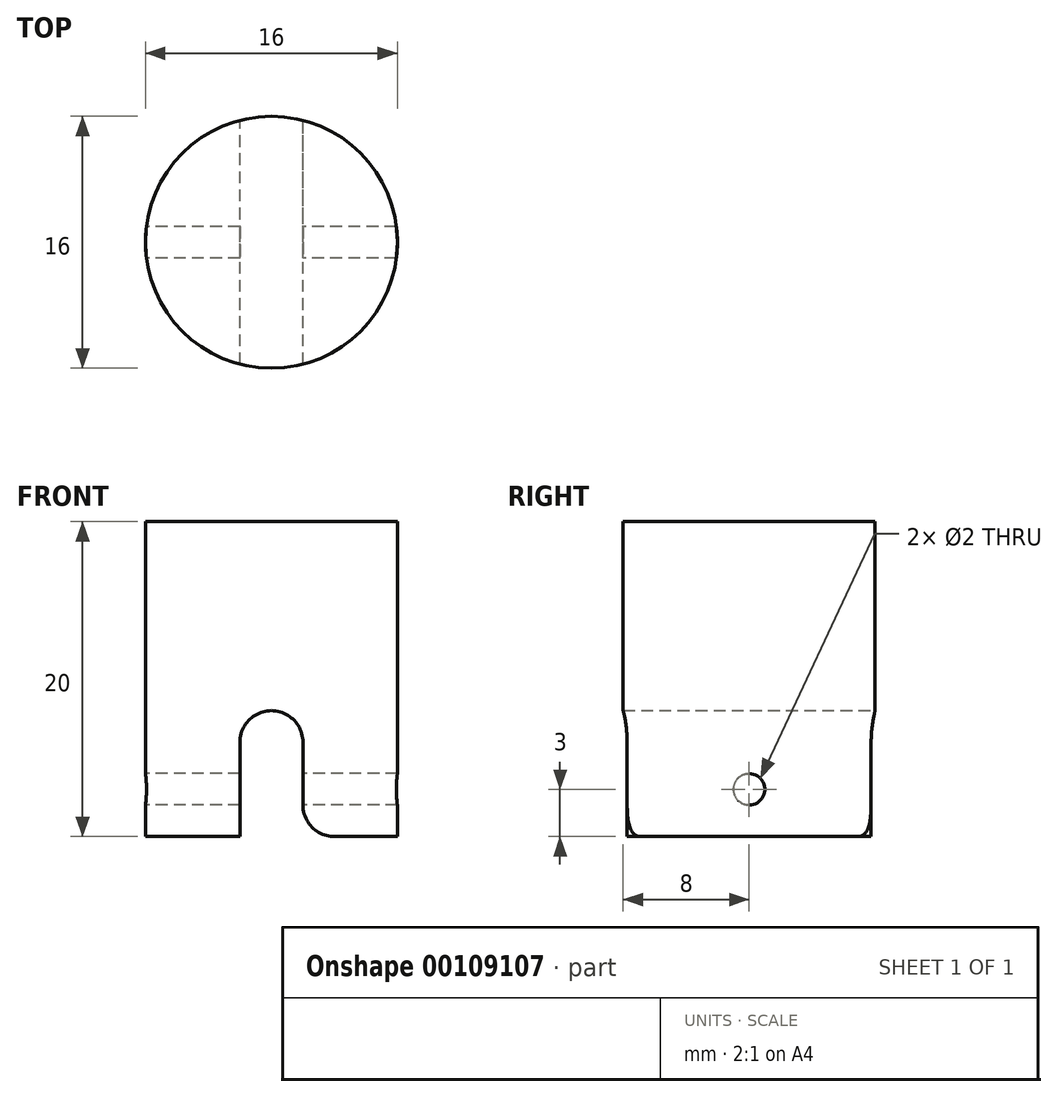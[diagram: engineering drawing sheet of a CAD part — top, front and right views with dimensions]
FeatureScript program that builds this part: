
annotation { "Feature Type Name" : "Feature", "Feature Type Description" : "" }
export const myFeature = defineFeature(function(context is Context, id is Id, definition is map)
    precondition{}
    {
        {
            var Q0;
            Q0=qCreatedBy(makeId("Top.planeOp"),FACE);
            var sketch = newSketch(context, id + "F0", { "sketchPlane" : qUnion([Q0])});
            skLineSegment(sketch, "E0.bottom", {"start": v(-8, 8) * mm, "end": v(8, 8) * mm});
            skLineSegment(sketch, "E0.top", {"start": v(-8, -8) * mm, "end": v(8, -8) * mm});
            skLineSegment(sketch, "E0.left", {"start": v(-8, 8) * mm, "end": v(-8, -8) * mm});
            skLineSegment(sketch, "E0.right", {"start": v(8, 8) * mm, "end": v(8, -8) * mm});
            skPoint(sketch, "E0.middle", {"position": v(0, 0) * mm});
            skSolve(sketch);
        }
        {
            var Q0;
            Q0=makeQuery(id+"F0.imprint","IMPRINT",FACE,{"disambiguationData":[TD([[makeQuery(id+"F0.imprint","IMPRINT",EDGE,{"derivedFrom":sQuery(id+"F0.wireOp",EDGE,"E0.bottom")}),-1.0]])]});
            extrude(context, id + "F1", {"entities" : qUnion([Q0]), "depth" : 20 * mm});
        }
        {
            var Q0;
            Q0=makeQuery(id+"F1.opExtrude","SWEPT_FACE",FACE,{"disambiguationData":[OSD([sQuery(id+"F0.wireOp",EDGE,"E0.left")])]});
            var sketch = newSketch(context, id + "F2", { "sketchPlane" : qUnion([Q0])});
            skLineSegment(sketch, "E1", {"start": v(0, 20) * mm, "end": v(0, 0) * mm});
            skCircle(sketch, "E2", {"center": v(0, 3) * mm, "radius": 1 * mm});
            skSolve(sketch);
        }
        {
            var Q0;
            Q0=sQuery(id+"F2.wireOp",VERTEX,"E2.center");
            var Q1;
            Q1=makeQuery(id+"F1.opExtrude","SWEPT_BODY",BODY,{"disambiguationData":[OSD([sQuery(id+"F0.wireOp",EDGE,"E0.bottom"),sQuery(id+"F0.wireOp",EDGE,"E0.top"),sQuery(id+"F0.wireOp",EDGE,"E0.left"),sQuery(id+"F0.wireOp",EDGE,"E0.right")])]});
            hole(context, id + "F3", {"style" : HoleStyle.SIMPLE, "endStyle" : HoleEndStyle.THROUGH, "holeDiameter" : 2 * mm, "locations" : qUnion([Q0]), "scope" : qUnion([Q1]), "isTappedThrough" : true});
        }
        {
            var Q0;
            Q0=makeQuery(id+"F1.opExtrude","CAP_FACE",FACE,{"disambiguationData":[OSD([sQuery(id+"F0.wireOp",EDGE,"E0.bottom"),sQuery(id+"F0.wireOp",EDGE,"E0.top"),sQuery(id+"F0.wireOp",EDGE,"E0.left"),sQuery(id+"F0.wireOp",EDGE,"E0.right")])],"isStart":false});
            var sketch = newSketch(context, id + "F4", { "sketchPlane" : qUnion([Q0])});
            skCircle(sketch, "E3", {"center": v(0, 0) * mm, "radius": 8 * mm});
            skSolve(sketch);
        }
        {
            var Q0;
            {var subQ0=sQuery(id+"F4.wireOp",EDGE,"E3");var subQ1=makeQuery(id+"F1.opExtrude","CAP_EDGE",EDGE,{"disambiguationData":[OSD([sQuery(id+"F0.wireOp",EDGE,"E0.bottom")])],"isStart":false});var subQ2=makeQuery(id+"F4.imprint","INTERSECT",VERTEX,{"derivedFrom":[subQ1,subQ0]});Q0=makeQuery(id+"F4.imprint","IMPRINT",FACE,{"disambiguationData":[TD([[makeQuery(id+"F4.imprint","IMPRINT",EDGE,{"disambiguationData":[TD([[subQ2,-1.0]])],"derivedFrom":subQ0}),-1.0]])]});}
            var Q1;
            {var subQ0=sQuery(id+"F4.wireOp",EDGE,"E3");var subQ1=makeQuery(id+"F1.opExtrude","CAP_EDGE",EDGE,{"disambiguationData":[OSD([sQuery(id+"F0.wireOp",EDGE,"E0.bottom")])],"isStart":false});var subQ2=makeQuery(id+"F4.imprint","INTERSECT",VERTEX,{"derivedFrom":[subQ1,subQ0]});Q1=makeQuery(id+"F4.imprint","IMPRINT",FACE,{"disambiguationData":[TD([[makeQuery(id+"F4.imprint","IMPRINT",EDGE,{"disambiguationData":[TD([[subQ2,1.0]])],"derivedFrom":subQ0}),-1.0]])]});}
            var Q2;
            {var subQ0=sQuery(id+"F4.wireOp",EDGE,"E3");var subQ1=makeQuery(id+"F1.opExtrude","CAP_EDGE",EDGE,{"disambiguationData":[OSD([sQuery(id+"F0.wireOp",EDGE,"E0.right")])],"isStart":false});var subQ2=makeQuery(id+"F4.imprint","INTERSECT",VERTEX,{"derivedFrom":[subQ1,subQ0]});Q2=makeQuery(id+"F4.imprint","IMPRINT",FACE,{"disambiguationData":[TD([[makeQuery(id+"F4.imprint","IMPRINT",EDGE,{"disambiguationData":[TD([[subQ2,1.0]])],"derivedFrom":subQ0}),-1.0]])]});}
            var Q3;
            {var subQ0=sQuery(id+"F4.wireOp",EDGE,"E3");var subQ1=makeQuery(id+"F1.opExtrude","CAP_EDGE",EDGE,{"disambiguationData":[OSD([sQuery(id+"F0.wireOp",EDGE,"E0.left")])],"isStart":false});var subQ2=makeQuery(id+"F4.imprint","INTERSECT",VERTEX,{"derivedFrom":[subQ1,subQ0]});Q3=makeQuery(id+"F4.imprint","IMPRINT",FACE,{"disambiguationData":[TD([[makeQuery(id+"F4.imprint","IMPRINT",EDGE,{"disambiguationData":[TD([[subQ2,-1.0]])],"derivedFrom":subQ0}),-1.0]])]});}
            extrude(context, id + "F5", {"entities" : qUnion([Q0, Q1, Q2, Q3]), "operationType" : NewBodyOperationType.REMOVE, "oppositeDirection" : true, "depth" : 20 * mm});
        }
        {
            var Q0;
            Q0=makeQuery(id+"F1.opExtrude","CAP_FACE",FACE,{"disambiguationData":[OSD([sQuery(id+"F0.wireOp",EDGE,"E0.bottom"),sQuery(id+"F0.wireOp",EDGE,"E0.top"),sQuery(id+"F0.wireOp",EDGE,"E0.left"),sQuery(id+"F0.wireOp",EDGE,"E0.right")])],"isStart":true});
            var sketch = newSketch(context, id + "F6", { "sketchPlane" : qUnion([Q0])});
            skLineSegment(sketch, "E4.bottom", {"start": v(-2, 7.75) * mm, "end": v(2, 7.75) * mm});
            skLineSegment(sketch, "E4.top", {"start": v(-2, -7.75) * mm, "end": v(2, -7.75) * mm});
            skLineSegment(sketch, "E4.left", {"start": v(-2, 7.75) * mm, "end": v(-2, -7.75) * mm});
            skLineSegment(sketch, "E4.right", {"start": v(2, 7.75) * mm, "end": v(2, -7.75) * mm});
            skPoint(sketch, "E4.middle", {"position": v(0, 0) * mm});
            skSolve(sketch);
        }
        {
            var Q0;
            {var subQ0=sQuery(id+"F6.wireOp",EDGE,"E4.bottom");Q0=makeQuery(id+"F6.imprint","IMPRINT",FACE,{"disambiguationData":[TD([[makeQuery(id+"F6.imprint","IMPRINT",EDGE,{"derivedFrom":subQ0}),1.0]])]});}
            var Q1;
            Q1=makeQuery(id+"F6.imprint","IMPRINT",FACE,{"disambiguationData":[TD([[makeQuery(id+"F6.imprint","IMPRINT",EDGE,{"derivedFrom":sQuery(id+"F6.wireOp",EDGE,"E4.bottom")}),-1.0]])]});
            var Q2;
            {var subQ0=sQuery(id+"F6.wireOp",EDGE,"E4.top");Q2=makeQuery(id+"F6.imprint","IMPRINT",FACE,{"disambiguationData":[TD([[makeQuery(id+"F6.imprint","IMPRINT",EDGE,{"derivedFrom":subQ0}),-1.0]])]});}
            extrude(context, id + "F7", {"entities" : qUnion([Q0, Q1, Q2]), "operationType" : NewBodyOperationType.REMOVE, "oppositeDirection" : true, "depth" : 8 * mm});
        }
        {
            var Q0;
            Q0=makeQuery(id+"F7.boolean.opBoolean","COPY",EDGE,{"derivedFrom":makeQuery(id+"F7.opExtrude","CAP_EDGE",EDGE,{"disambiguationData":[OSD([sQuery(id+"F6.wireOp",EDGE,"E4.left")])],"isStart":true})});
            var Q1;
            Q1=makeQuery(id+"F7.boolean.opBoolean","COPY",EDGE,{"derivedFrom":makeQuery(id+"F7.opExtrude","CAP_EDGE",EDGE,{"disambiguationData":[OSD([sQuery(id+"F6.wireOp",EDGE,"E4.right")])],"isStart":true})});
            fillet(context, id + "F8", {"entities" : qUnion([Q0, Q1]), "radius" : 2 * mm, "tangentPropagation" : true, "allowEdgeOverflow" : false});
        }
        {
            var Q0;
            Q0=makeQuery(id+"F7.boolean.opBoolean","COPY",EDGE,{"derivedFrom":makeQuery(id+"F7.opExtrude","CAP_EDGE",EDGE,{"disambiguationData":[OSD([sQuery(id+"F6.wireOp",EDGE,"E4.left")])],"isStart":false})});
            var Q1;
            Q1=makeQuery(id+"F7.boolean.opBoolean","COPY",EDGE,{"derivedFrom":makeQuery(id+"F7.opExtrude","CAP_EDGE",EDGE,{"disambiguationData":[OSD([sQuery(id+"F6.wireOp",EDGE,"E4.right")])],"isStart":false})});
            fillet(context, id + "F9", {"entities" : qUnion([Q0, Q1]), "radius" : 2 * mm, "tangentPropagation" : true, "allowEdgeOverflow" : false});
        }
    });
